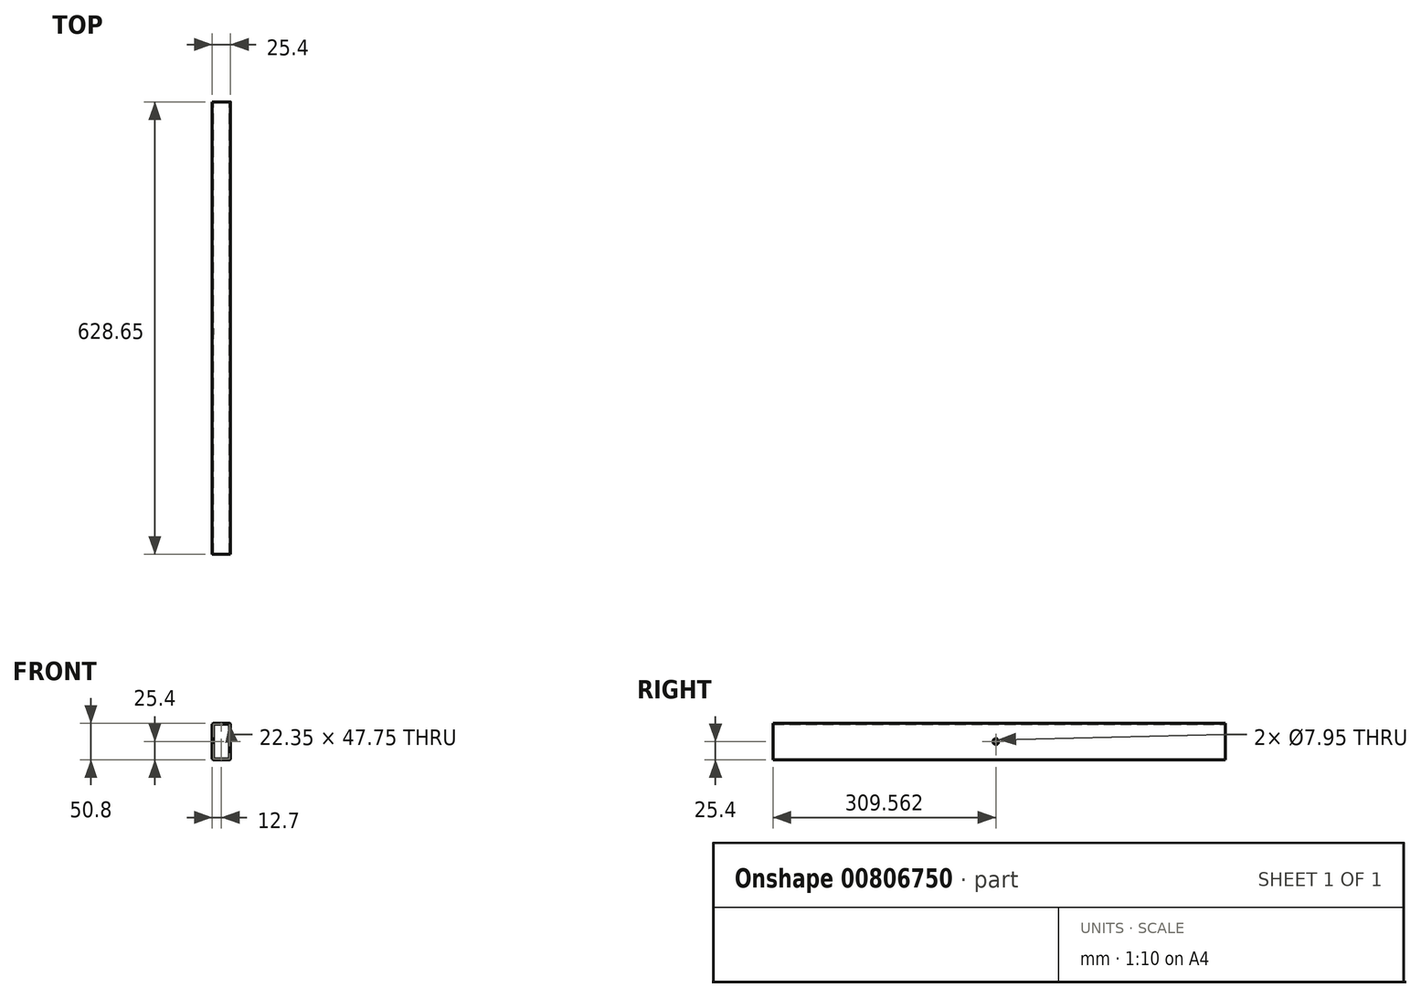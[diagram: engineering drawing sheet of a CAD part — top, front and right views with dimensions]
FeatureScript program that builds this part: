
annotation { "Feature Type Name" : "Feature", "Feature Type Description" : "" }
export const myFeature = defineFeature(function(context is Context, id is Id, definition is map)
    precondition{}
    {
        {
            var Q0;
            Q0=qCreatedBy(makeId("Front.planeOp"),FACE);
            var sketch = newSketch(context, id + "F0", { "sketchPlane" : qUnion([Q0])});
            skLineSegment(sketch, "E0.bottom", {"start": v(1.52, 0) * mm, "end": v(23.88, 0) * mm});
            skLineSegment(sketch, "E0.top", {"start": v(1.52, 50.8) * mm, "end": v(23.88, 50.8) * mm});
            skLineSegment(sketch, "E0.left", {"start": v(0, 1.52) * mm, "end": v(0, 49.28) * mm});
            skLineSegment(sketch, "E0.right", {"start": v(25.4, 1.52) * mm, "end": v(25.4, 49.28) * mm});
            skPoint(sketch, "E1.visualSharp", {"position": v(0, 50.8) * mm});
            skArc(sketch, "E1.filletArc", {"start": v(1.52, 50.8) * mm, "mid": v(0.45, 50.35) * mm, "end": v(0, 49.28) * mm});
            skPoint(sketch, "E2.visualSharp", {"position": v(25.4, 50.8) * mm});
            skArc(sketch, "E2.filletArc", {"start": v(25.4, 49.28) * mm, "mid": v(24.95, 50.35) * mm, "end": v(23.88, 50.8) * mm});
            skPoint(sketch, "E3.visualSharp", {"position": v(25.4, 0) * mm});
            skArc(sketch, "E3.filletArc", {"start": v(23.88, 0) * mm, "mid": v(24.95, 0.45) * mm, "end": v(25.4, 1.52) * mm});
            skPoint(sketch, "E4.visualSharp", {"position": v(0, 0) * mm});
            skArc(sketch, "E4.filletArc", {"start": v(0, 1.52) * mm, "mid": v(0.45, 0.45) * mm, "end": v(1.52, 0) * mm});
            skLineSegment(sketch, "E5.0", {"start": v(23.88, 1.52) * mm, "end": v(23.88, 49.28) * mm});
            skLineSegment(sketch, "E5.1", {"start": v(1.52, 1.52) * mm, "end": v(23.88, 1.52) * mm});
            skLineSegment(sketch, "E5.2", {"start": v(1.52, 1.52) * mm, "end": v(1.52, 49.28) * mm});
            skLineSegment(sketch, "E5.3", {"start": v(1.52, 49.28) * mm, "end": v(23.88, 49.28) * mm});
            skSolve(sketch);
        }
        {
            var Q0;
            Q0 = qSketchRegion(id + "F0", true);
            extrude(context, id + "F1", {"entities" : qUnion([Q0]), "depth" : 628.65 * mm, "offsetDistance" : 25.4 * mm});
        }
        {
            var Q0;
            Q0=makeQuery(id+"F1.opExtrude","SWEPT_FACE",FACE,{"disambiguationData":[OSD([sQuery(id+"F0.wireOp",EDGE,"E0.right")])]});
            var sketch = newSketch(context, id + "F2", { "sketchPlane" : qUnion([Q0])});
            skCircle(sketch, "E6", {"center": v(-319.09, 25.4) * mm, "radius": 3.98 * mm});
            skSolve(sketch);
        }
        {
            var Q0;
            Q0 = qSketchRegion(id + "F2", true);
            extrude(context, id + "F3", {"entities" : qUnion([Q0]), "operationType" : NewBodyOperationType.REMOVE, "endBound" : BoundingType.THROUGH_ALL, "oppositeDirection" : true, "depth" : 25.4 * mm, "offsetDistance" : 25.4 * mm});
        }
    });
